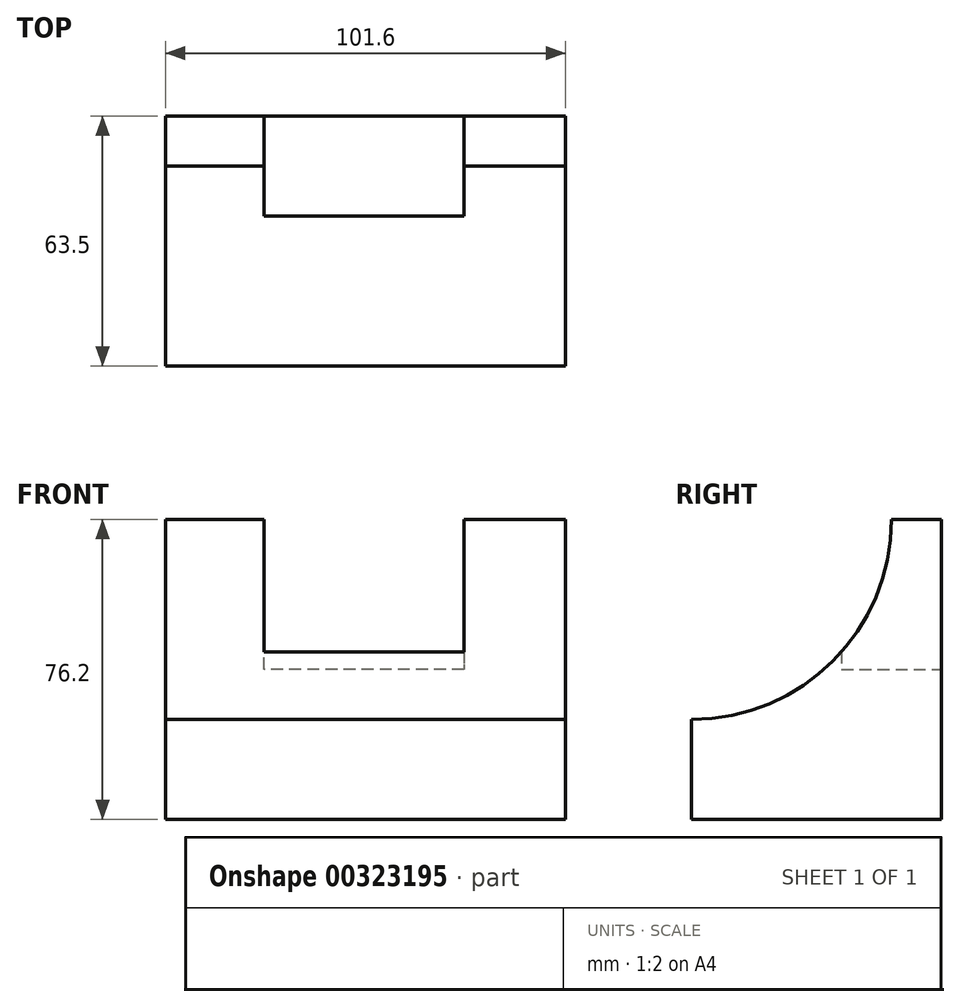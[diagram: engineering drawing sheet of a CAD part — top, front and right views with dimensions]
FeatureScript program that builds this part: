
annotation { "Feature Type Name" : "Feature", "Feature Type Description" : "" }
export const myFeature = defineFeature(function(context is Context, id is Id, definition is map)
    precondition{}
    {
        {
            var Q0;
            Q0=qCreatedBy(makeId("Front.planeOp"),FACE);
            var sketch = newSketch(context, id + "F0", { "sketchPlane" : qUnion([Q0])});
            skLineSegment(sketch, "E0", {"start": v(-55.56, 15.88) * mm, "end": v(-55.56, -60.32) * mm});
            skLineSegment(sketch, "E1", {"start": v(-55.56, -60.32) * mm, "end": v(46.04, -60.32) * mm});
            skLineSegment(sketch, "E2", {"start": v(46.04, -60.32) * mm, "end": v(46.04, 15.88) * mm});
            skLineSegment(sketch, "E3", {"start": v(46.04, 15.88) * mm, "end": v(-55.56, 15.88) * mm});
            skSolve(sketch);
        }
        {
            var Q0;
            Q0=makeQuery(id+"F0.imprint","IMPRINT",FACE,{"disambiguationData":[TD([[makeQuery(id+"F0.imprint","IMPRINT",EDGE,{"derivedFrom":sQuery(id+"F0.wireOp",EDGE,"E0")}),1.0]])]});
            extrude(context, id + "F1", {"entities" : qUnion([Q0]), "depth" : 63.5 * mm});
        }
        {
            var Q0;
            Q0=makeQuery(id+"F1.opExtrude","SWEPT_FACE",FACE,{"disambiguationData":[OSD([sQuery(id+"F0.wireOp",EDGE,"E2")])]});
            var sketch = newSketch(context, id + "F2", { "sketchPlane" : qUnion([Q0])});
            skCircle(sketch, "E4", {"center": v(-63.5, 15.88) * mm, "radius": 50.8 * mm});
            skSolve(sketch);
        }
        {
            var Q0;
            {var subQ0=sQuery(id+"F2.wireOp",EDGE,"E4");var subQ1=sQuery(id+"F0.wireOp",EDGE,"E2");var subQ4=makeQuery(id+"F1.opExtrude","CAP_EDGE",EDGE,{"disambiguationData":[OSD([subQ1])],"isStart":false});var subQ5=makeQuery(id+"F2.imprint","INTERSECT",VERTEX,{"derivedFrom":[subQ4,subQ0]});Q0=makeQuery(id+"F2.imprint","IMPRINT",FACE,{"disambiguationData":[TD([[makeQuery(id+"F2.imprint","IMPRINT",EDGE,{"disambiguationData":[TD([[subQ5,-1.0]])],"derivedFrom":subQ0}),1.0]])]});}
            extrude(context, id + "F3", {"entities" : qUnion([Q0]), "operationType" : NewBodyOperationType.REMOVE, "oppositeDirection" : true, "depth" : 101.6 * mm});
        }
        {
            var Q0;
            Q0=makeQuery(id+"F1.opExtrude","CAP_FACE",FACE,{"disambiguationData":[OSD([sQuery(id+"F0.wireOp",EDGE,"E0"),sQuery(id+"F0.wireOp",EDGE,"E1"),sQuery(id+"F0.wireOp",EDGE,"E2"),sQuery(id+"F0.wireOp",EDGE,"E3")])],"isStart":true});
            var sketch = newSketch(context, id + "F4", { "sketchPlane" : qUnion([Q0])});
            skLineSegment(sketch, "E5", {"start": v(-20.26, 15.88) * mm, "end": v(-20.26, -22.22) * mm});
            skLineSegment(sketch, "E6", {"start": v(-20.26, -22.22) * mm, "end": v(30.54, -22.22) * mm});
            skLineSegment(sketch, "E7", {"start": v(30.54, -22.22) * mm, "end": v(30.54, 15.88) * mm});
            skSolve(sketch);
        }
        {
            var Q0;
            {var subQ0=sQuery(id+"F4.wireOp",EDGE,"E5");Q0=makeQuery(id+"F4.imprint","IMPRINT",FACE,{"disambiguationData":[TD([[makeQuery(id+"F4.imprint","IMPRINT",EDGE,{"derivedFrom":subQ0}),1.0]])]});}
            extrude(context, id + "F5", {"entities" : qUnion([Q0]), "operationType" : NewBodyOperationType.REMOVE, "oppositeDirection" : true, "depth" : 25.4 * mm});
        }
    });
